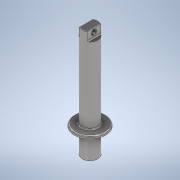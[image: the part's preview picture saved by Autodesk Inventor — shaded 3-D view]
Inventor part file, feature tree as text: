
AUTODESK INVENTOR PART (.ipt)
format: ipt  version: 2022 (Build 260153000, 153)  size: 187,392 bytes
history: native  units: in
note: dims shown in document units (in); Inventor stores cm internally (conversion verified against a paired STEP export)
features: fillet x4, sketch x3, revolve x1, extrude x1, hole x1
ambient origin geometry x8: Origin, YZ Plane, XZ Plane, XY Plane, X Axis, Y Axis, Z Axis, Center Point
bodies: Solid1 (feature_tree)
feature tree (10):
  revolve  "Revolution1"  [1 undecoded]
  fillet  "Fillet1"  Radius=3.937in
  extrude  "Extrusion1"  Depth=0.1969in
  fillet  "Fillet2"  Radius=0.1969in
  fillet  "Fillet3"  Radius=0.3937in
  hole  "Hole1"  [1 undecoded]
  fillet  "Fillet4"  [1 undecoded]
  sketch  "Sketch1"  dims[d0=0.9843in d1=0.1969in d2=3.937in]
  sketch  "Sketch2"  dims[d3=0.9843in d4=0.1969in d5=0.1969in d6=0.3937in]
  sketch  "Sketch3"  dims[d7=11.4173in d8=9.8425in d9=360.0deg d10=0.1969in d11=0.5906in d12=1.1811in d13=1.378in d14=0.0in d15=0.0787in d16=0.1969in d17=0.7874in d18=0.7874in d19=0.2362in d20=0.1575in d21=0.0787in d22=90.0deg d23=0.315in d24=0.8108in d25=0.0787in]
note: 3 required parameter values undecoded (feature->parameter linkage not recoverable at this tier; creation-order binding heuristic only, values carry confidence <= 0.55)